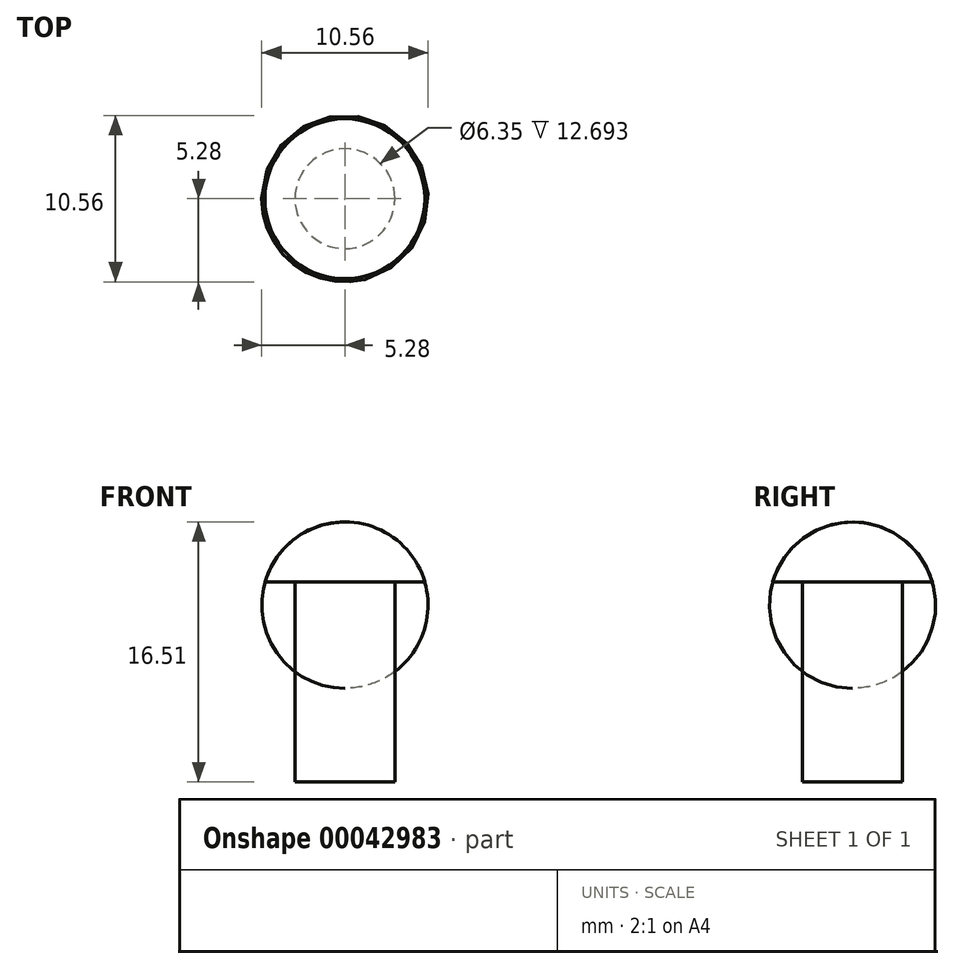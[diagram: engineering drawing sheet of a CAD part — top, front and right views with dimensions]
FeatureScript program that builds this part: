
annotation { "Feature Type Name" : "Feature", "Feature Type Description" : "" }
export const myFeature = defineFeature(function(context is Context, id is Id, definition is map)
    precondition{}
    {
        {
            var Q0;
            Q0=qCreatedBy(makeId("Front.planeOp"),FACE);
            var sketch = newSketch(context, id + "F0", { "sketchPlane" : qUnion([Q0])});
            skLineSegment(sketch, "E0", {"start": v(0, 0) * mm, "end": v(0, 16.5) * mm});
            skLineSegment(sketch, "E1", {"start": v(0, 16.5) * mm, "end": v(0, 0) * mm});
            skLineSegment(sketch, "E2", {"start": v(0, 0) * mm, "end": v(3.17, 0) * mm});
            skLineSegment(sketch, "E3", {"start": v(3.17, 0) * mm, "end": v(3.17, 12.7) * mm});
            skLineSegment(sketch, "E4", {"start": v(0, 12.7) * mm, "end": v(5.08, 12.7) * mm});
            skArc(sketch, "E5", {"start": v(5.08, 12.7) * mm, "mid": v(3.18, 15.45) * mm, "end": v(0, 16.51) * mm});
            skSolve(sketch);
        }
        {
            var Q0;
            Q0 = qSketchRegion(id + "F0", true);
            var Q1;
            Q1=sQuery(id+"F0.wireOp",EDGE,"E1");
            revolve(context, id + "F1", {"entities" : qUnion([Q0]), "axis" : qUnion([Q1]), "revolveType" : RevolveType.FULL});
        }
    });
